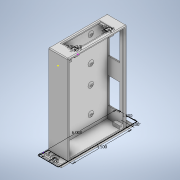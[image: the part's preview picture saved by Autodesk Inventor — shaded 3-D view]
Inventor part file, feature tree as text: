
AUTODESK INVENTOR PART (.ipt)
format: ipt  version: 2020 (Build 240168000, 168)  size: 480,768 bytes
history: native  units: in
note: dims shown in document units (in); Inventor stores cm internally (conversion verified against a paired STEP export)
features: sketch x14, extrude x13, fillet x5, hole x4, pattern_linear x2, thread x1
ambient origin geometry x8: Origin, YZ Plane, XZ Plane, XY Plane, X Axis, Y Axis, Z Axis, Center Point
bodies: Solid1 (feature_tree)
feature tree (39):
  sketch  "Sketch1"  dims[d0=1.5in d1=6.0in]
  extrude  "Extrusion1"  Depth=6.0in
  extrude  "Extrusion2"  Depth=4.5in
  hole  "Hole1"  [1 undecoded]
  extrude  "Extrusion7"  Depth=0.1875in
  extrude  "Extrusion8"  Depth=0.1875in
  extrude  "Extrusion3"  Depth=0.125in
  extrude  "Extrusion4"  Depth=0.125in
  extrude  "Extrusion5"  Depth=0.125in TaperAngle=0.0deg
  extrude  "Extrusion6"  Depth=0.25in
  extrude  "Extrusion9"  Depth=0.5in
  hole  "Hole2"  [1 undecoded]
  thread  "Thread1"  [1 undecoded]
  pattern_linear  "Rectangular Pattern1"  Spacing1=2.2835in  [1 undecoded]
  hole  "Hole4"  [1 undecoded]
  fillet  "Fillet1"  Radius=0.5in
  extrude  "Extrusion11"  Depth=0.125in TaperAngle=0.0deg
  extrude  "Extrusion12"  Depth=0.125in
  sketch  "Sketch18"  dims[d36=0.9252in]
  extrude  "Extrusion13"  Depth=0.0787in TaperAngle=0.0deg
  hole  "Hole6"  [1 undecoded]
  fillet  "Fillet2"  Radius=0.1875in
  fillet  "Fillet3"  Radius=0.125in
  pattern_linear  "Rectangular Pattern3"  Spacing1=0.125in  [1 undecoded]
  fillet  "Fillet4"  Radius=0.0625in
  extrude  "Extrusion18"  Depth=0.125in
  fillet  "Fillet5"  Radius=0.75in
  sketch  "Sketch2"  dims[d2=0.75in d3=4.5in]
  sketch  "Sketch3"  dims[d4=0.1875in d5=0.0in d6=6.75in d7=0.0in]
  sketch  "Sketch4"  dims[d8=0.5in]
  sketch  "Sketch5"  dims[d9=0.266in d10=0.75in d11=0.507in d12=0.0625in d13=0.5635in d14=1.0in d15=0.8108in d16=0.1875in]
  sketch  "Sketch6"  dims[d17=0.1875in d18=0.1875in]
  sketch  "Sketch7"  dims[d19=1.3125in d20=0.0in d21=0.125in]
  sketch  "Sketch8"  dims[d22=0.125in d23=0.125in]
  sketch  "Sketch9"  dims[d24=0.125in d25=0.125in d26=0.0in]
  sketch  "Sketch12"  dims[d27=0.5in d28=0.25in]
  sketch  "Sketch16"  dims[d29=0.25in d30=0.0in d31=0.5in]
  sketch  "Sketch17"  dims[d32=0.25in d33=0.25in d34=0.0in d35=0.5906in]
  sketch  "Sketch30"  dims[d37=1.9291in d38=2.2835in d39=0.25in d40=0.0in d41=0.5in d43=0.25in d44=0.0in d45=0.1969in d46=0.0787in d47=0.0in d48=0.0807in d49=0.197in d50=0.119in d51=0.188in d52=90.0deg d53=0.25in d54=0.8108in d55=0.25in d56=0.0in d57=0.7874in d59=2.2835in d60=0.7874in d62=1.9291in d82=0.1875in d83=0.1875in d84=0.125in d85=0.125in d86=0.089in d87=0.146in d88=0.119in d89=0.188in d90=0.5635in d91=0.224in d92=0.8108in d93=0.0625in d128=2.75in d130=0.75in d131=0.0in d132=1.0in d133=3.0in d134=0.0625in d135=0.0in d136=1.5in d137=0.5in d138=90.0deg d139=0.75in d140=2.75in d141=0.125in d142=0.0in d143=0.375in d144=0.375in d145=0.375in d146=0.375in d147=0.375in d148=0.0in d149=0.1875in d150=0.1875in d151=0.1875in d152=0.1875in d153=0.089in d154=0.197in d155=0.119in d156=0.188in d157=0.5635in d158=0.259in d159=0.8108in d160=0.0625in d198=0.125in d206=0.3779in d224=0.3779in d244=0.3779in d262=0.3779in d273=0.7874in d275=3.3465in d276=0.125in d277=0.875in d278=0.875in d279=1.0in d280=0.0in d281=0.125in]
note: 7 required parameter values undecoded (feature->parameter linkage not recoverable at this tier; creation-order binding heuristic only, values carry confidence <= 0.55)
